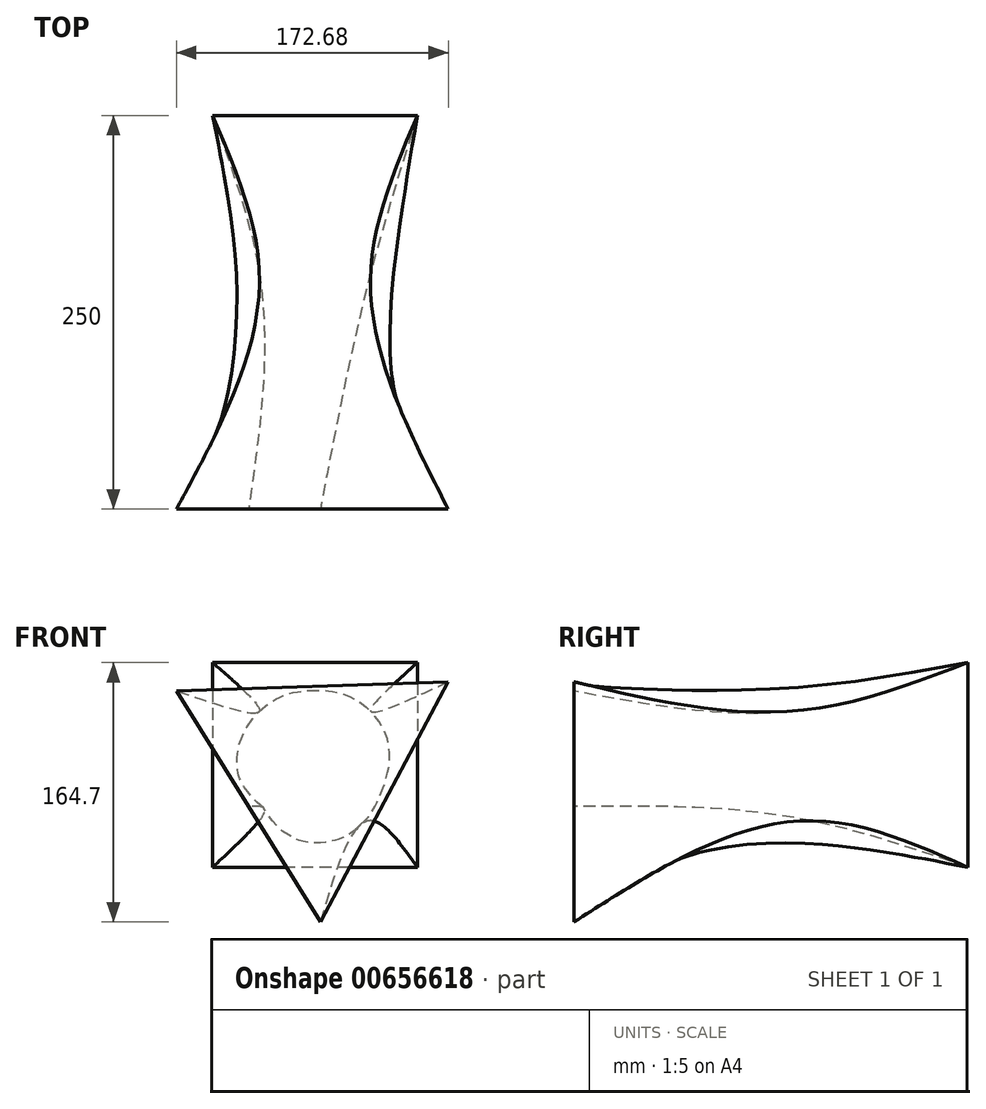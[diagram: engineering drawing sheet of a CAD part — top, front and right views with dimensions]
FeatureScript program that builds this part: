
annotation { "Feature Type Name" : "Feature", "Feature Type Description" : "" }
export const myFeature = defineFeature(function(context is Context, id is Id, definition is map)
    precondition{}
    {
        {
            var Q0;
            Q0=qCreatedBy(makeId("Front.planeOp"),FACE);
            cPlane(context, id + "F0", {"entities" : qUnion([Q0]), "cplaneType" : CPlaneType.OFFSET, "offset" : 100 * mm, "width" : 150 * mm, "height" : 150 * mm});
        }
        {
            var Q0;
            Q0=qCreatedBy(id+"F0.planeOp",FACE);
            var sketch = newSketch(context, id + "F1", { "sketchPlane" : qUnion([Q0])});
            skCircle(sketch, "E0", {"center": v(0, 0) * mm, "radius": 50 * mm});
            skSolve(sketch);
        }
        {
            var Q0;
            Q0=qCreatedBy(makeId("Front.planeOp"),FACE);
            var sketch = newSketch(context, id + "F2", { "sketchPlane" : qUnion([Q0])});
            skLineSegment(sketch, "E1.bottom", {"start": v(65, 65) * mm, "end": v(-65, 65) * mm});
            skLineSegment(sketch, "E1.top", {"start": v(65, -65) * mm, "end": v(-65, -65) * mm});
            skLineSegment(sketch, "E1.left", {"start": v(65, 65) * mm, "end": v(65, -65) * mm});
            skLineSegment(sketch, "E1.right", {"start": v(-65, 65) * mm, "end": v(-65, -65) * mm});
            skPoint(sketch, "E1.middle", {"position": v(0, 0) * mm});
            skSolve(sketch);
        }
        {
            var Q0;
            Q0=qCreatedBy(id+"F0.planeOp",FACE);
            cPlane(context, id + "F3", {"entities" : qUnion([Q0]), "cplaneType" : CPlaneType.OFFSET, "offset" : 150 * mm, "width" : 150 * mm, "height" : 150 * mm});
        }
        {
            var Q0;
            Q0=qCreatedBy(id+"F3.planeOp",FACE);
            var sketch = newSketch(context, id + "F4", { "sketchPlane" : qUnion([Q0])});
            skCircle(sketch, "E2.cCircle", {"center": v(0, 0) * mm, "radius": 49.88 * mm, "construction": true});
            skLineSegment(sketch, "E2.0", {"start": v(-88.05, 46.88) * mm, "end": v(84.63, 52.81) * mm});
            skLineSegment(sketch, "E2.1", {"start": v(84.63, 52.81) * mm, "end": v(3.42, -99.7) * mm});
            skLineSegment(sketch, "E2.2", {"start": v(3.42, -99.7) * mm, "end": v(-88.05, 46.88) * mm});
            skPoint(sketch, "E2.0.midPoint", {"position": v(-1.71, 49.85) * mm});
            skSolve(sketch);
        }
        {
            var Q0;
            Q0=makeQuery(id+"F2.imprint","IMPRINT",FACE,{"disambiguationData":[TD([[makeQuery(id+"F2.imprint","IMPRINT",EDGE,{"derivedFrom":sQuery(id+"F2.wireOp",EDGE,"E1.bottom")}),1.0]])]});
            var Q1;
            Q1=makeQuery(id+"F1.imprint","IMPRINT",FACE,{"disambiguationData":[TD([[makeQuery(id+"F1.imprint","IMPRINT",EDGE,{"derivedFrom":sQuery(id+"F1.wireOp",EDGE,"E0")}),1.0]])]});
            var Q2;
            Q2=makeQuery(id+"F4.imprint","IMPRINT",FACE,{"disambiguationData":[TD([[makeQuery(id+"F4.imprint","IMPRINT",EDGE,{"derivedFrom":sQuery(id+"F4.wireOp",EDGE,"E2.0")}),-1.0]])]});
            loft(context, id + "F5", {"sheetProfilesArray" : [{ "sheetProfileEntities" : qUnion([Q0]) }, { "sheetProfileEntities" : qUnion([Q1]) }, { "sheetProfileEntities" : qUnion([Q2]) }]});
        }
    });
